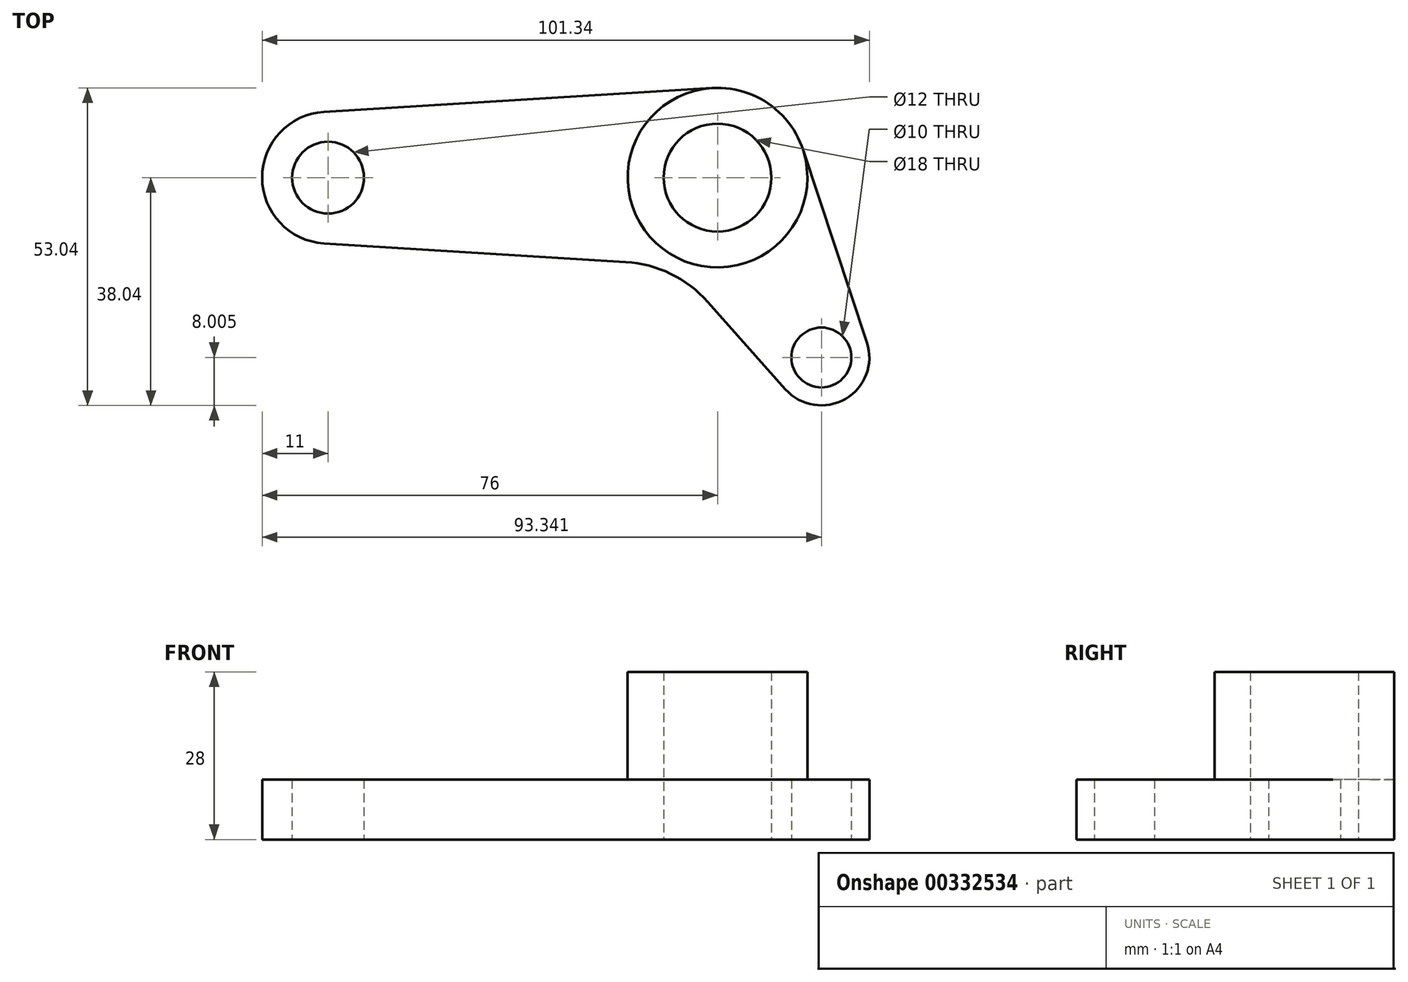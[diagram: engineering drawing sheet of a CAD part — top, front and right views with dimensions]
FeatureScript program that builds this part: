
annotation { "Feature Type Name" : "Feature", "Feature Type Description" : "" }
export const myFeature = defineFeature(function(context is Context, id is Id, definition is map)
    precondition{}
    {
        {
            var Q0;
            Q0=qCreatedBy(makeId("Top.planeOp"),FACE);
            var sketch = newSketch(context, id + "F0", { "sketchPlane" : qUnion([Q0])});
            skCircle(sketch, "E0", {"center": v(0, 0) * mm, "radius": 9 * mm});
            skCircle(sketch, "E1", {"center": v(0, 0) * mm, "radius": 15 * mm});
            skCircle(sketch, "E2", {"center": v(17.34, -30.04) * mm, "radius": 5 * mm});
            skArc(sketch, "E3", {"start": v(11.36, -35.35) * mm, "mid": v(21.34, -36.96) * mm, "end": v(24.93, -27.52) * mm});
            skCircle(sketch, "E4", {"center": v(-65, 0) * mm, "radius": 6 * mm});
            skArc(sketch, "E5", {"start": v(-65.68, 10.98) * mm, "mid": v(-76, 0) * mm, "end": v(-65.68, -10.98) * mm});
            skLineSegment(sketch, "E6", {"start": v(-65.68, 10.98) * mm, "end": v(-0.92, 14.97) * mm});
            skLineSegment(sketch, "E7", {"start": v(14.24, 4.72) * mm, "end": v(24.93, -27.52) * mm});
            skLineSegment(sketch, "E8", {"start": v(11.36, -35.35) * mm, "end": v(-1.62, -20.76) * mm});
            skLineSegment(sketch, "E9", {"start": v(-65.68, -10.98) * mm, "end": v(-15.33, -14.08) * mm});
            skArc(sketch, "E10", {"start": v(-1.62, -20.76) * mm, "mid": v(-7.81, -16.06) * mm, "end": v(-15.33, -14.08) * mm});
            skSolve(sketch);
        }
        {
            var Q0;
            Q0=makeQuery(id+"F0.imprint","IMPRINT",FACE,{"disambiguationData":[TD([[makeQuery(id+"F0.imprint","IMPRINT",EDGE,{"derivedFrom":sQuery(id+"F0.wireOp",EDGE,"E2")}),-1.0]])]});
            var Q1;
            Q1=makeQuery(id+"F0.imprint","IMPRINT",FACE,{"disambiguationData":[TD([[makeQuery(id+"F0.imprint","IMPRINT",EDGE,{"derivedFrom":sQuery(id+"F0.wireOp",EDGE,"E0")}),-1.0]])]});
            extrude(context, id + "F1", {"entities" : qUnion([Q0, Q1]), "depth" : 10 * mm});
        }
        {
            var Q0;
            Q0=makeQuery(id+"F0.imprint","IMPRINT",FACE,{"disambiguationData":[TD([[makeQuery(id+"F0.imprint","IMPRINT",EDGE,{"derivedFrom":sQuery(id+"F0.wireOp",EDGE,"E0")}),-1.0]])]});
            extrude(context, id + "F2", {"entities" : qUnion([Q0]), "operationType" : NewBodyOperationType.ADD, "depth" : 28 * mm});
        }
    });
